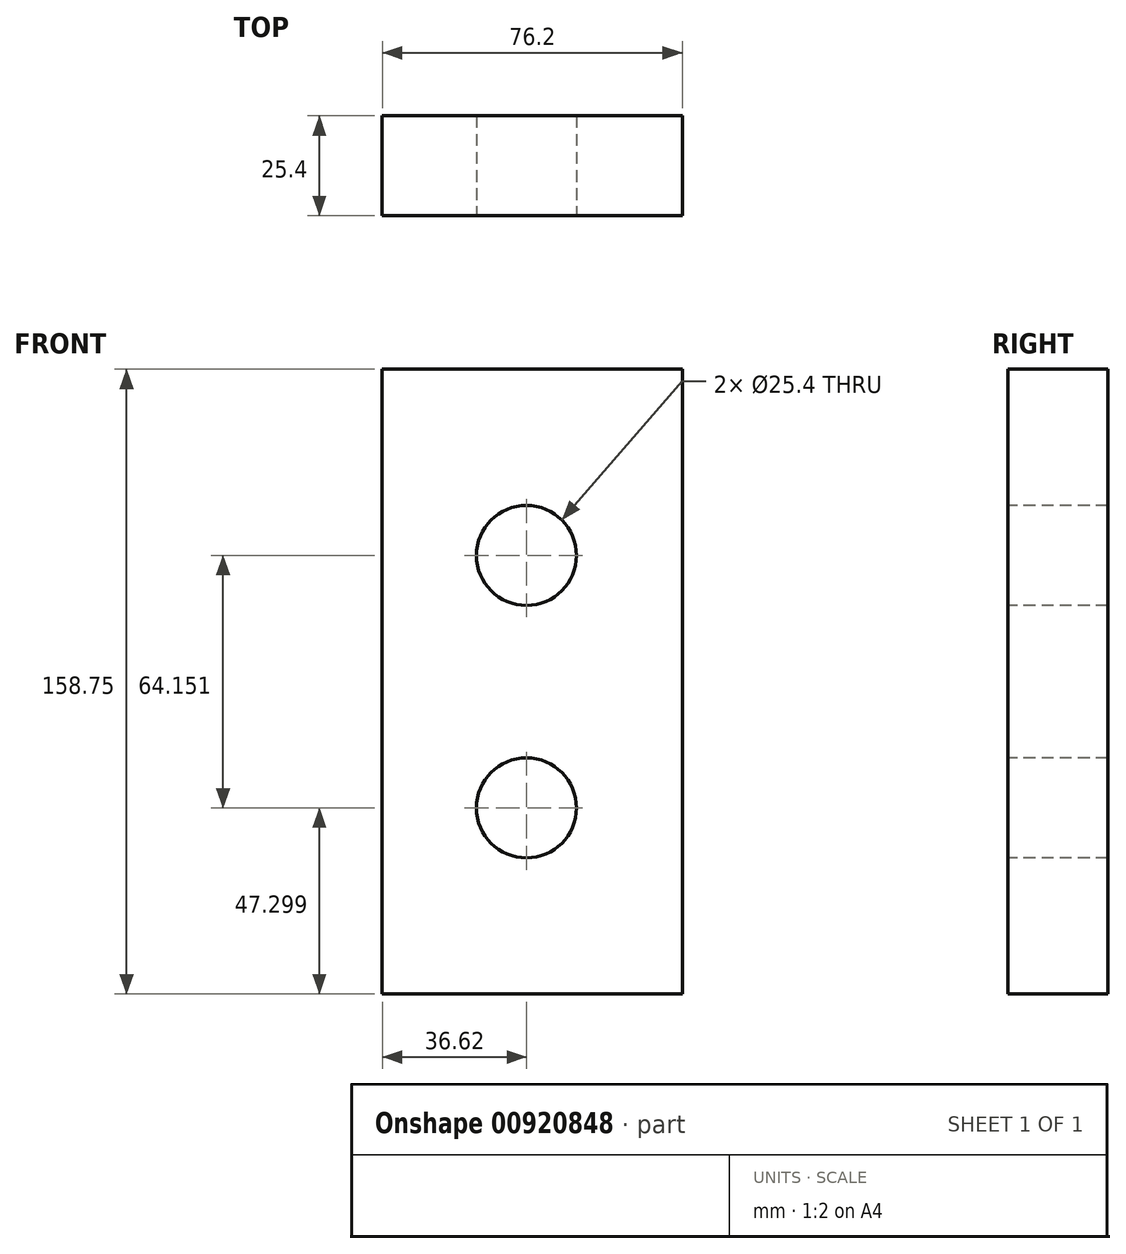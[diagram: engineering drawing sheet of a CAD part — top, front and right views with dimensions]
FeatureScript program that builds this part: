
annotation { "Feature Type Name" : "Feature", "Feature Type Description" : "" }
export const myFeature = defineFeature(function(context is Context, id is Id, definition is map)
    precondition{}
    {
        {
            var Q0;
            Q0=qCreatedBy(makeId("Top.planeOp"),FACE);
            var sketch = newSketch(context, id + "F0", { "sketchPlane" : qUnion([Q0])});
            skLineSegment(sketch, "E0.bottom", {"start": v(-36.62, 12.7) * mm, "end": v(39.58, 12.7) * mm});
            skLineSegment(sketch, "E0.top", {"start": v(-36.62, -12.7) * mm, "end": v(39.58, -12.7) * mm});
            skLineSegment(sketch, "E0.left", {"start": v(-36.62, 12.7) * mm, "end": v(-36.62, -12.7) * mm});
            skLineSegment(sketch, "E0.right", {"start": v(39.58, 12.7) * mm, "end": v(39.58, -12.7) * mm});
            skPoint(sketch, "E0.middle", {"position": v(1.48, 0) * mm});
            skSolve(sketch);
        }
        {
            var Q0;
            Q0 = qSketchRegion(id + "F0", true);
            extrude(context, id + "F1", {"entities" : qUnion([Q0]), "depth" : 158.75 * mm, "offsetDistance" : 25.4 * mm});
        }
        {
            var Q0;
            Q0=makeQuery(id+"F1.opExtrude","SWEPT_FACE",FACE,{"disambiguationData":[OSD([sQuery(id+"F0.wireOp",EDGE,"E0.top")])]});
            var sketch = newSketch(context, id + "F2", { "sketchPlane" : qUnion([Q0])});
            skLineSegment(sketch, "E1", {"start": v(0, 0) * mm, "end": v(0, 158.75) * mm, "construction": true});
            skCircle(sketch, "E2", {"center": v(0, 111.45) * mm, "radius": 12.7 * mm});
            skCircle(sketch, "E3", {"center": v(0, 47.3) * mm, "radius": 12.7 * mm});
            skLineSegment(sketch, "E4", {"start": v(-36.62, 79.38) * mm, "end": v(39.58, 79.38) * mm, "construction": true});
            skSolve(sketch);
        }
        {
            var Q0;
            Q0 = qSketchRegion(id + "F2", true);
            extrude(context, id + "F3", {"entities" : qUnion([Q0]), "operationType" : NewBodyOperationType.REMOVE, "oppositeDirection" : true, "depth" : 25.4 * mm, "offsetDistance" : 25.4 * mm});
        }
    });
